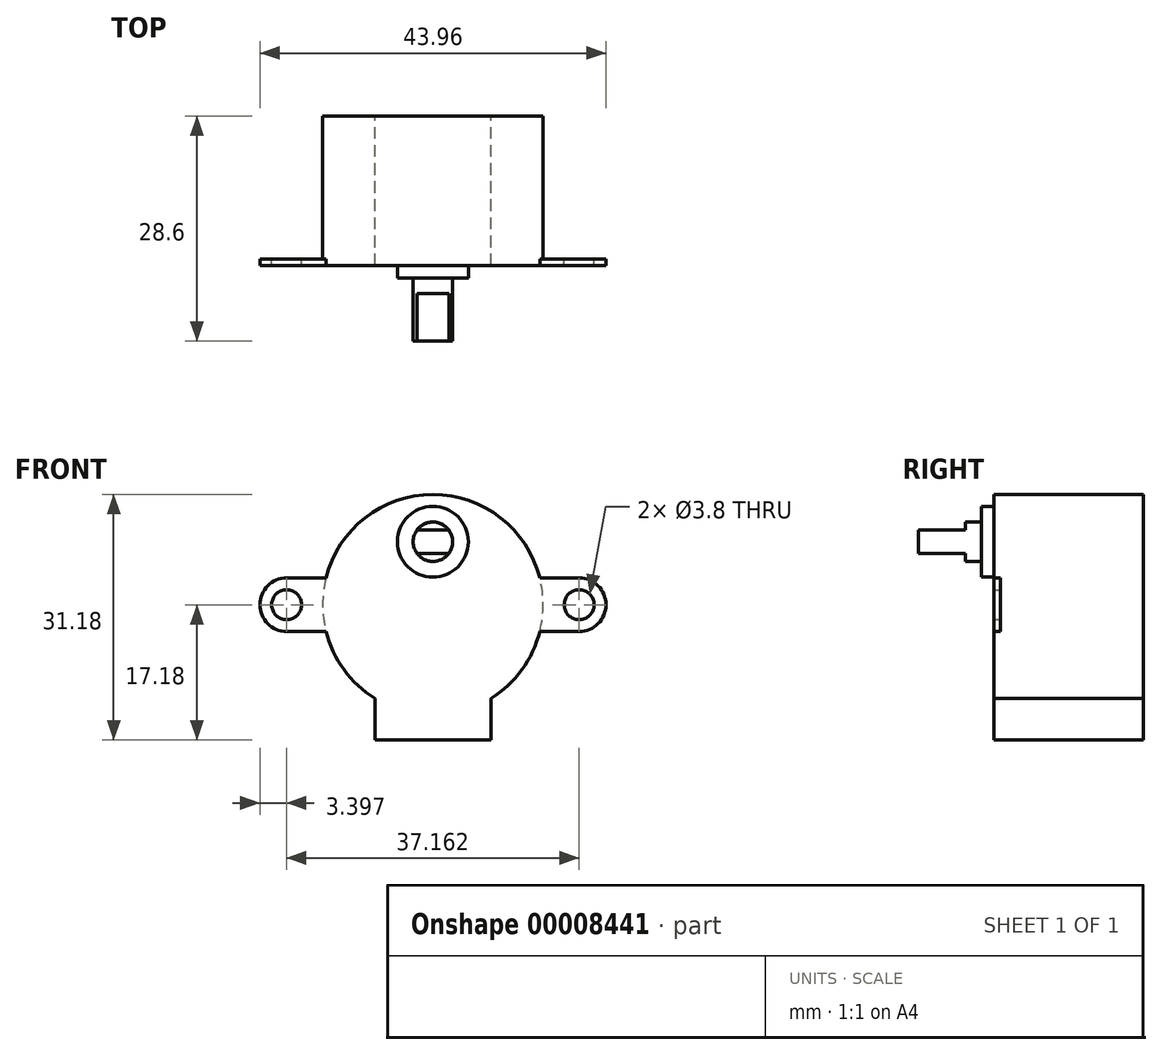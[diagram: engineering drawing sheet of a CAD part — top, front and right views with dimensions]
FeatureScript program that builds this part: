
annotation { "Feature Type Name" : "Feature", "Feature Type Description" : "" }
export const myFeature = defineFeature(function(context is Context, id is Id, definition is map)
    precondition{}
    {
        {
            var Q0;
            Q0=qCreatedBy(makeId("Front.planeOp"),FACE);
            var sketch = newSketch(context, id + "F0", { "sketchPlane" : qUnion([Q0])});
            skCircle(sketch, "E0", {"center": v(-15.98, 11.9) * mm, "radius": 14 * mm});
            skCircle(sketch, "E1", {"center": v(-34.56, 11.9) * mm, "radius": 1.9 * mm});
            skCircle(sketch, "E2", {"center": v(2.6, 11.9) * mm, "radius": 1.9 * mm});
            skLineSegment(sketch, "E3", {"start": v(-23.36, 0) * mm, "end": v(-23.36, -5.28) * mm});
            skLineSegment(sketch, "E4", {"start": v(-23.36, -5.28) * mm, "end": v(-8.6, -5.28) * mm});
            skLineSegment(sketch, "E5", {"start": v(-8.6, -5.28) * mm, "end": v(-8.6, 0) * mm});
            skPoint(sketch, "E6", {"position": v(-15.98, -5.28) * mm});
            skArc(sketch, "E7", {"start": v(-34.56, 15.3) * mm, "mid": v(-37.96, 11.9) * mm, "end": v(-34.56, 8.5) * mm});
            skArc(sketch, "E8", {"start": v(2.6, 8.5) * mm, "mid": v(6, 11.9) * mm, "end": v(2.6, 15.3) * mm});
            skLineSegment(sketch, "E9", {"start": v(2.6, 15.3) * mm, "end": v(-2.4, 15.3) * mm});
            skLineSegment(sketch, "E10", {"start": v(2.6, 8.5) * mm, "end": v(-2.4, 8.5) * mm});
            skLineSegment(sketch, "E11", {"start": v(-34.56, 8.5) * mm, "end": v(-29.56, 8.5) * mm});
            skLineSegment(sketch, "E12", {"start": v(-34.56, 15.3) * mm, "end": v(-29.56, 15.3) * mm});
            skSolve(sketch);
        }
        {
            var Q0;
            {var subQ0=sQuery(id+"F0.wireOp",EDGE,"E0");var subQ2=makeQuery(id+"F0.imprint","INTERSECT",VERTEX,{"derivedFrom":[subQ0,sQuery(id+"F0.wireOp",EDGE,"E9")]});Q0=makeQuery(id+"F0.imprint","IMPRINT",FACE,{"disambiguationData":[TD([[makeQuery(id+"F0.imprint","IMPRINT",EDGE,{"disambiguationData":[TD([[subQ2,-1.0]])],"derivedFrom":subQ0}),1.0]])]});}
            var Q1;
            Q1=makeQuery(id+"F0.imprint","IMPRINT",FACE,{"disambiguationData":[TD([[makeQuery(id+"F0.imprint","IMPRINT",EDGE,{"derivedFrom":sQuery(id+"F0.wireOp",EDGE,"E1")}),-1.0]])]});
            var Q2;
            {var subQ1=sQuery(id+"F0.wireOp",EDGE,"E3");Q2=makeQuery(id+"F0.imprint","IMPRINT",FACE,{"disambiguationData":[TD([[makeQuery(id+"F0.imprint","IMPRINT",EDGE,{"derivedFrom":subQ1}),1.0]])]});}
            var Q3;
            Q3=makeQuery(id+"F0.imprint","IMPRINT",FACE,{"disambiguationData":[TD([[makeQuery(id+"F0.imprint","IMPRINT",EDGE,{"derivedFrom":sQuery(id+"F0.wireOp",EDGE,"E2")}),-1.0]])]});
            extrude(context, id + "F1", {"entities" : qUnion([Q0, Q1, Q2, Q3]), "depth" : 0.8 * mm});
        }
        {
            var Q0;
            Q0=makeQuery(id+"F1.opExtrude","CAP_FACE",FACE,{"disambiguationData":[OSD([sQuery(id+"F0.wireOp",EDGE,"E0"),sQuery(id+"F0.wireOp",EDGE,"E1"),sQuery(id+"F0.wireOp",EDGE,"E2"),sQuery(id+"F0.wireOp",EDGE,"E3"),sQuery(id+"F0.wireOp",EDGE,"E4"),sQuery(id+"F0.wireOp",EDGE,"E5"),sQuery(id+"F0.wireOp",EDGE,"E7"),sQuery(id+"F0.wireOp",EDGE,"E8"),sQuery(id+"F0.wireOp",EDGE,"E9"),sQuery(id+"F0.wireOp",EDGE,"E10"),sQuery(id+"F0.wireOp",EDGE,"E11"),sQuery(id+"F0.wireOp",EDGE,"E12")])],"isStart":true});
            var sketch = newSketch(context, id + "F2", { "sketchPlane" : qUnion([Q0])});
            skPoint(sketch, "E13", {"position": v(15.98, 11.9) * mm});
            skPoint(sketch, "E14", {"position": v(15.98, 25.9) * mm});
            skPoint(sketch, "E15", {"position": v(8.6, -5.28) * mm});
            skPoint(sketch, "E16", {"position": v(8.6, 0) * mm});
            skPoint(sketch, "E17", {"position": v(23.36, 0) * mm});
            skPoint(sketch, "E18", {"position": v(23.36, -5.28) * mm});
            skCircle(sketch, "E19", {"center": v(15.98, 11.9) * mm, "radius": 14 * mm});
            skLineSegment(sketch, "E20", {"start": v(8.6, 0) * mm, "end": v(8.6, -5.28) * mm});
            skLineSegment(sketch, "E21", {"start": v(8.6, -5.28) * mm, "end": v(23.36, -5.28) * mm});
            skLineSegment(sketch, "E22", {"start": v(23.36, -5.28) * mm, "end": v(23.36, 0) * mm});
            skSolve(sketch);
        }
        {
            var Q0;
            {var subQ0=sQuery(id+"F2.wireOp",EDGE,"E19");var subQ1=makeQuery(id+"F2.imprint","INTERSECT",VERTEX,{"derivedFrom":[makeQuery(id+"F1.opExtrude","CAP_EDGE",EDGE,{"disambiguationData":[OSD([sQuery(id+"F0.wireOp",EDGE,"E12")])],"isStart":true}),subQ0]});var subQ6=makeQuery(id+"F2.imprint","INTERSECT",VERTEX,{"derivedFrom":[makeQuery(id+"F1.opExtrude","CAP_EDGE",EDGE,{"disambiguationData":[OSD([sQuery(id+"F0.wireOp",EDGE,"E9")])],"isStart":true}),subQ0]});Q0=makeQuery(id+"F2.imprint","IMPRINT",FACE,{"disambiguationData":[TD([[makeQuery(id+"F2.imprint","IMPRINT",EDGE,{"disambiguationData":[TD([[subQ6,-1.0],[subQ1,1.0]])],"derivedFrom":subQ0}),-1.0]])]});}
            var Q1;
            {var subQ1=sQuery(id+"F2.wireOp",EDGE,"E20");Q1=makeQuery(id+"F2.imprint","IMPRINT",FACE,{"disambiguationData":[TD([[makeQuery(id+"F2.imprint","IMPRINT",EDGE,{"derivedFrom":subQ1}),-1.0]])]});}
            extrude(context, id + "F3", {"entities" : qUnion([Q0, Q1]), "operationType" : NewBodyOperationType.ADD, "depth" : 18.2 * mm});
        }
        {
            var Q0;
            Q0=makeQuery(id+"F1.opExtrude","CAP_FACE",FACE,{"disambiguationData":[OSD([sQuery(id+"F0.wireOp",EDGE,"E0"),sQuery(id+"F0.wireOp",EDGE,"E1"),sQuery(id+"F0.wireOp",EDGE,"E2"),sQuery(id+"F0.wireOp",EDGE,"E3"),sQuery(id+"F0.wireOp",EDGE,"E4"),sQuery(id+"F0.wireOp",EDGE,"E5"),sQuery(id+"F0.wireOp",EDGE,"E7"),sQuery(id+"F0.wireOp",EDGE,"E8"),sQuery(id+"F0.wireOp",EDGE,"E9"),sQuery(id+"F0.wireOp",EDGE,"E10"),sQuery(id+"F0.wireOp",EDGE,"E11"),sQuery(id+"F0.wireOp",EDGE,"E12")])],"isStart":false});
            var sketch = newSketch(context, id + "F4", { "sketchPlane" : qUnion([Q0])});
            skPoint(sketch, "E23", {"position": v(-15.98, 11.9) * mm});
            skPoint(sketch, "E24", {"position": v(-15.98, 25.9) * mm});
            skPoint(sketch, "E25", {"position": v(-15.98, 19.9) * mm});
            skCircle(sketch, "E26", {"center": v(-15.98, 19.9) * mm, "radius": 4.5 * mm});
            skSolve(sketch);
        }
        {
            var Q0;
            Q0=makeQuery(id+"F4.imprint","IMPRINT",FACE,{"disambiguationData":[TD([[makeQuery(id+"F4.imprint","IMPRINT",EDGE,{"derivedFrom":sQuery(id+"F4.wireOp",EDGE,"E26")}),1.0]])]});
            extrude(context, id + "F5", {"entities" : qUnion([Q0]), "operationType" : NewBodyOperationType.ADD, "depth" : 1.6 * mm});
        }
        {
            var Q0;
            Q0=makeQuery(id+"F5.opExtrude","CAP_FACE",FACE,{"disambiguationData":[OSD([sQuery(id+"F4.wireOp",EDGE,"E26")])],"isStart":false});
            var sketch = newSketch(context, id + "F6", { "sketchPlane" : qUnion([Q0])});
            skPoint(sketch, "E27", {"position": v(-15.98, 19.9) * mm});
            skCircle(sketch, "E28", {"center": v(-15.98, 19.9) * mm, "radius": 2.5 * mm});
            skSolve(sketch);
        }
        {
            var Q0;
            Q0=makeQuery(id+"F6.imprint","IMPRINT",FACE,{"disambiguationData":[TD([[makeQuery(id+"F6.imprint","IMPRINT",EDGE,{"derivedFrom":sQuery(id+"F6.wireOp",EDGE,"E28")}),1.0]])]});
            extrude(context, id + "F7", {"entities" : qUnion([Q0]), "operationType" : NewBodyOperationType.ADD, "depth" : 2 * mm});
        }
        {
            var Q0;
            Q0=makeQuery(id+"F7.opExtrude","CAP_FACE",FACE,{"disambiguationData":[OSD([sQuery(id+"F6.wireOp",EDGE,"E28")])],"isStart":false});
            var sketch = newSketch(context, id + "F8", { "sketchPlane" : qUnion([Q0])});
            skPoint(sketch, "E29", {"position": v(-15.98, 19.9) * mm});
            skPoint(sketch, "E30", {"position": v(-15.98, 22.4) * mm});
            skLineSegment(sketch, "E31", {"start": v(-18, 21.37) * mm, "end": v(-13.96, 21.37) * mm});
            skLineSegment(sketch, "E32", {"start": v(-13.96, 18.42) * mm, "end": v(-18, 18.42) * mm});
            skSolve(sketch);
        }
        {
            var Q0;
            {var subQ2=sQuery(id+"F8.wireOp",EDGE,"E31");Q0=makeQuery(id+"F8.imprint","IMPRINT",FACE,{"disambiguationData":[TD([[makeQuery(id+"F8.imprint","IMPRINT",EDGE,{"derivedFrom":subQ2}),-1.0]])]});}
            extrude(context, id + "F9", {"entities" : qUnion([Q0]), "operationType" : NewBodyOperationType.ADD, "depth" : 6 * mm});
        }
    });
